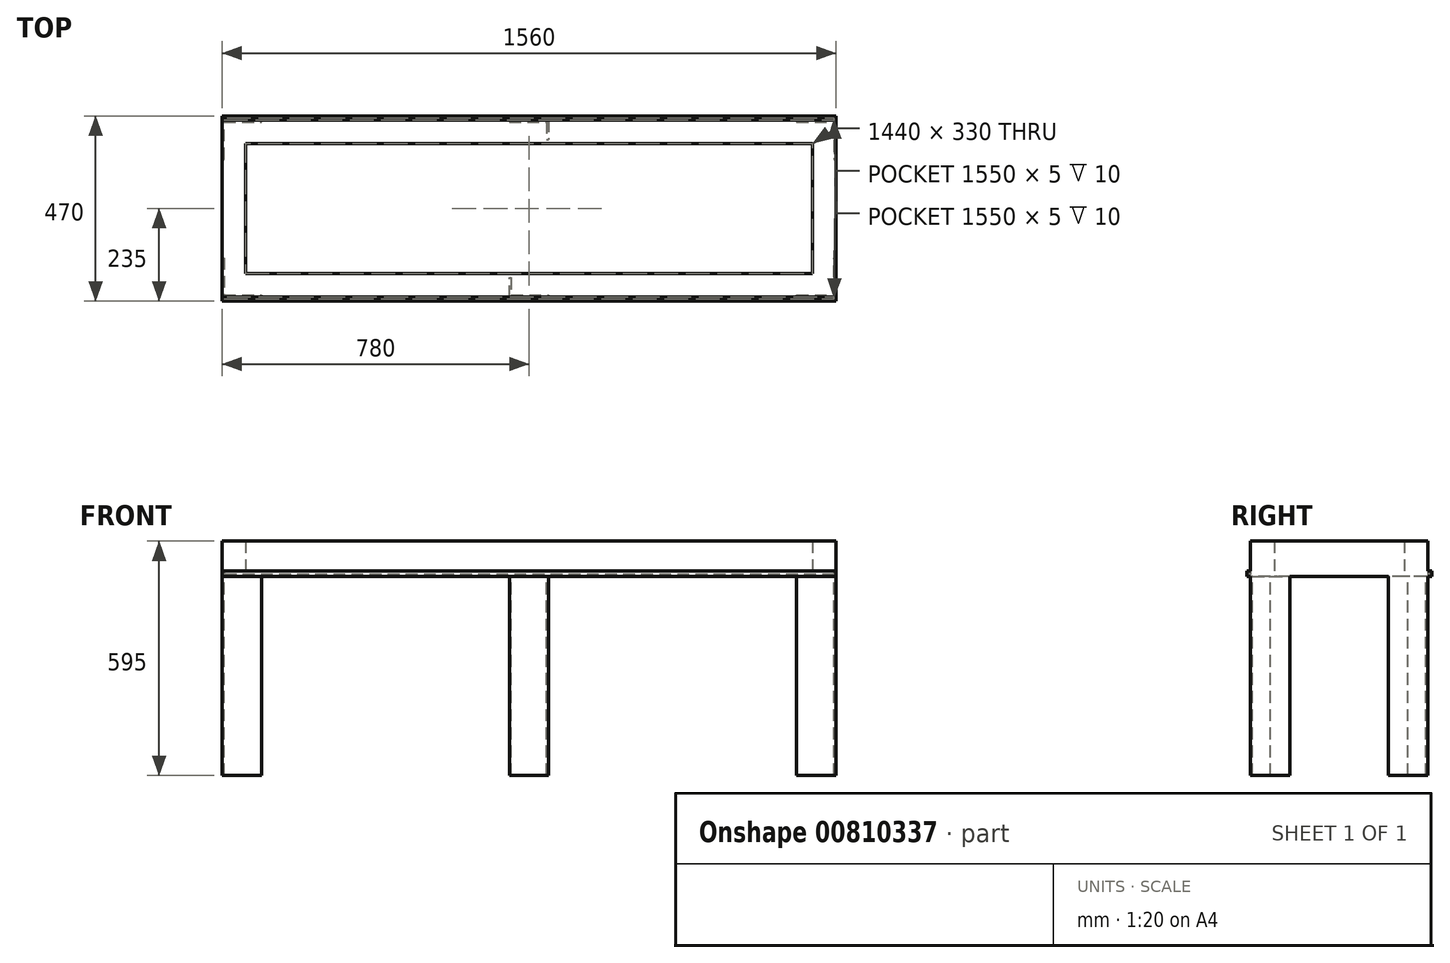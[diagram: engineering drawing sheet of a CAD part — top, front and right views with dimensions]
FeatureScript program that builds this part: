
annotation { "Feature Type Name" : "Feature", "Feature Type Description" : "" }
export const myFeature = defineFeature(function(context is Context, id is Id, definition is map)
    precondition{}
    {
        {
            var Q0;
            Q0=qCreatedBy(makeId("Top.planeOp"),FACE);
            var sketch = newSketch(context, id + "F0", { "sketchPlane" : qUnion([Q0])});
            skLineSegment(sketch, "E0", {"start": v(0, 526.95) * mm, "end": v(0, -464.95) * mm, "construction": true});
            skLineSegment(sketch, "E1", {"start": v(-587.5, 0) * mm, "end": v(637.96, 0) * mm, "construction": true});
            skLineSegment(sketch, "E2.bottom", {"start": v(-780, 225) * mm, "end": v(780, 225) * mm});
            skLineSegment(sketch, "E2.top", {"start": v(-780, -225) * mm, "end": v(780, -225) * mm});
            skLineSegment(sketch, "E2.left", {"start": v(-780, 225) * mm, "end": v(-780, -225) * mm});
            skLineSegment(sketch, "E2.right", {"start": v(780, 225) * mm, "end": v(780, -225) * mm});
            skLineSegment(sketch, "E3.0", {"start": v(-720, -165) * mm, "end": v(720, -165) * mm});
            skLineSegment(sketch, "E3.1", {"start": v(-720, 165) * mm, "end": v(-720, -165) * mm});
            skLineSegment(sketch, "E3.2", {"start": v(-720, 165) * mm, "end": v(720, 165) * mm});
            skLineSegment(sketch, "E3.3", {"start": v(720, 165) * mm, "end": v(720, -165) * mm});
            skSolve(sketch);
        }
        {
            var Q0;
            Q0 = qSketchRegion(id + "F0", true);
            extrude(context, id + "F1", {"entities" : qUnion([Q0]), "depth" : 90 * mm, "offsetDistance" : 25.4 * mm});
        }
        {
            var Q0;
            Q0=makeQuery(id+"F1.opExtrude","CAP_FACE",FACE,{"disambiguationData":[OSD([sQuery(id+"F0.wireOp",EDGE,"E2.bottom"),sQuery(id+"F0.wireOp",EDGE,"E2.top"),sQuery(id+"F0.wireOp",EDGE,"E2.left"),sQuery(id+"F0.wireOp",EDGE,"E2.right")])],"isStart":true});
            var sketch = newSketch(context, id + "F2", { "sketchPlane" : qUnion([Q0])});
            skLineSegment(sketch, "E4", {"start": v(-780, 125) * mm, "end": v(-780, 225) * mm});
            skLineSegment(sketch, "E5", {"start": v(-780, 225) * mm, "end": v(-680, 225) * mm});
            skLineSegment(sketch, "E6", {"start": v(-780, 125) * mm, "end": v(-775, 125) * mm});
            skLineSegment(sketch, "E7", {"start": v(-775, 125) * mm, "end": v(-775, 220) * mm});
            skLineSegment(sketch, "E8", {"start": v(-775, 220) * mm, "end": v(-680, 220) * mm});
            skLineSegment(sketch, "E9", {"start": v(-680, 220) * mm, "end": v(-680, 225) * mm});
            skLineSegment(sketch, "E10", {"start": v(-780, -125) * mm, "end": v(-780, -225) * mm});
            skLineSegment(sketch, "E11", {"start": v(-780, -225) * mm, "end": v(-680, -225) * mm});
            skLineSegment(sketch, "E12", {"start": v(-780, -125) * mm, "end": v(-775, -125) * mm});
            skLineSegment(sketch, "E13", {"start": v(-775, -125) * mm, "end": v(-775, -220) * mm});
            skLineSegment(sketch, "E14", {"start": v(-775, -220) * mm, "end": v(-680, -220) * mm});
            skLineSegment(sketch, "E15", {"start": v(-680, -220) * mm, "end": v(-680, -225) * mm});
            skLineSegment(sketch, "E16", {"start": v(0, 284.77) * mm, "end": v(0, -302.96) * mm, "construction": true});
            skLineSegment(sketch, "E17", {"start": v(-50, 225) * mm, "end": v(50, 225) * mm});
            skLineSegment(sketch, "E18", {"start": v(-50, 225) * mm, "end": v(-50, 175) * mm});
            skLineSegment(sketch, "E19", {"start": v(-50, 175) * mm, "end": v(-45, 175) * mm});
            skLineSegment(sketch, "E20", {"start": v(-45, 175) * mm, "end": v(-45, 220) * mm});
            skLineSegment(sketch, "E21", {"start": v(-45, 220) * mm, "end": v(50, 220) * mm});
            skLineSegment(sketch, "E22", {"start": v(50, 220) * mm, "end": v(50, 225) * mm});
            skLineSegment(sketch, "E23", {"start": v(-50, -225) * mm, "end": v(50, -225) * mm});
            skLineSegment(sketch, "E24", {"start": v(50, -225) * mm, "end": v(50, -175) * mm});
            skLineSegment(sketch, "E25", {"start": v(-50, -225) * mm, "end": v(-50, -220) * mm});
            skLineSegment(sketch, "E26", {"start": v(-50, -220) * mm, "end": v(45, -220) * mm});
            skLineSegment(sketch, "E27", {"start": v(45, -220) * mm, "end": v(45, -175) * mm});
            skLineSegment(sketch, "E28", {"start": v(45, -175) * mm, "end": v(50, -175) * mm});
            skLineSegment(sketch, "E29", {"start": v(680, 225) * mm, "end": v(780, 225) * mm});
            skLineSegment(sketch, "E30", {"start": v(780, 225) * mm, "end": v(780, 125) * mm});
            skLineSegment(sketch, "E31", {"start": v(680, 225) * mm, "end": v(680, 220) * mm});
            skLineSegment(sketch, "E32", {"start": v(680, 220) * mm, "end": v(775, 220) * mm});
            skLineSegment(sketch, "E33", {"start": v(775, 220) * mm, "end": v(775, 125) * mm});
            skLineSegment(sketch, "E34", {"start": v(775, 125) * mm, "end": v(780, 125) * mm});
            skLineSegment(sketch, "E35", {"start": v(680, -225) * mm, "end": v(780, -225) * mm});
            skLineSegment(sketch, "E36", {"start": v(780, -225) * mm, "end": v(780, -125) * mm});
            skLineSegment(sketch, "E37", {"start": v(680, -225) * mm, "end": v(680, -220) * mm});
            skLineSegment(sketch, "E38", {"start": v(680, -220) * mm, "end": v(775, -220) * mm});
            skLineSegment(sketch, "E39", {"start": v(775, -220) * mm, "end": v(775, -125) * mm});
            skLineSegment(sketch, "E40", {"start": v(775, -125) * mm, "end": v(780, -125) * mm});
            skSolve(sketch);
        }
        {
            var Q0;
            Q0 = qSketchRegion(id + "F2", true);
            extrude(context, id + "F3", {"entities" : qUnion([Q0]), "operationType" : NewBodyOperationType.ADD, "depth" : 505 * mm, "offsetDistance" : 25.4 * mm});
        }
        {
            var Q0;
            Q0=makeQuery(id+"F3.boolean.opBoolean","MERGE",FACE,{"derivedFrom":[makeQuery(id+"F1.opExtrude","SWEPT_FACE",FACE,{"disambiguationData":[OSD([sQuery(id+"F0.wireOp",EDGE,"E2.top")])]}),makeQuery(id+"F3.opExtrude","SWEPT_FACE",FACE,{"disambiguationData":[OSD([sQuery(id+"F2.wireOp",EDGE,"E5")])]}),makeQuery(id+"F3.opExtrude","SWEPT_FACE",FACE,{"disambiguationData":[OSD([sQuery(id+"F2.wireOp",EDGE,"E17")])]}),makeQuery(id+"F3.opExtrude","SWEPT_FACE",FACE,{"disambiguationData":[OSD([sQuery(id+"F2.wireOp",EDGE,"E29")])]})]});
            var sketch = newSketch(context, id + "F4", { "sketchPlane" : qUnion([Q0])});
            skLineSegment(sketch, "E41.bottom", {"start": v(-780, 0) * mm, "end": v(780, 0) * mm});
            skLineSegment(sketch, "E41.top", {"start": v(-780, 5) * mm, "end": v(780, 5) * mm});
            skLineSegment(sketch, "E41.left", {"start": v(-780, 0) * mm, "end": v(-780, 5) * mm});
            skLineSegment(sketch, "E41.right", {"start": v(780, 0) * mm, "end": v(780, 5) * mm});
            skSolve(sketch);
        }
        {
            var Q0;
            Q0=makeQuery(id+"F3.boolean.opBoolean","MERGE",FACE,{"derivedFrom":[makeQuery(id+"F1.opExtrude","SWEPT_FACE",FACE,{"disambiguationData":[OSD([sQuery(id+"F0.wireOp",EDGE,"E2.bottom")])]}),makeQuery(id+"F3.opExtrude","SWEPT_FACE",FACE,{"disambiguationData":[OSD([sQuery(id+"F2.wireOp",EDGE,"E11")])]}),makeQuery(id+"F3.opExtrude","SWEPT_FACE",FACE,{"disambiguationData":[OSD([sQuery(id+"F2.wireOp",EDGE,"E23")])]}),makeQuery(id+"F3.opExtrude","SWEPT_FACE",FACE,{"disambiguationData":[OSD([sQuery(id+"F2.wireOp",EDGE,"E35")])]})]});
            var sketch = newSketch(context, id + "F5", { "sketchPlane" : qUnion([Q0])});
            skLineSegment(sketch, "E42.bottom", {"start": v(-780, 0) * mm, "end": v(780, 0) * mm});
            skLineSegment(sketch, "E42.top", {"start": v(-780, 5) * mm, "end": v(780, 5) * mm});
            skLineSegment(sketch, "E42.left", {"start": v(-780, 0) * mm, "end": v(-780, 5) * mm});
            skLineSegment(sketch, "E42.right", {"start": v(780, 0) * mm, "end": v(780, 5) * mm});
            skSolve(sketch);
        }
        {
            var Q0;
            Q0 = qSketchRegion(id + "F4", true);
            extrude(context, id + "F6", {"entities" : qUnion([Q0]), "operationType" : NewBodyOperationType.ADD, "depth" : 10 * mm, "offsetDistance" : 25.4 * mm});
        }
        {
            var Q0;
            Q0 = qSketchRegion(id + "F5", true);
            extrude(context, id + "F7", {"entities" : qUnion([Q0]), "operationType" : NewBodyOperationType.ADD, "depth" : 10 * mm, "offsetDistance" : 25.4 * mm});
        }
        {
            var Q0;
            Q0=makeQuery(id+"F6.opExtrude","SWEPT_FACE",FACE,{"disambiguationData":[OSD([sQuery(id+"F4.wireOp",EDGE,"E41.top")])]});
            var sketch = newSketch(context, id + "F8", { "sketchPlane" : qUnion([Q0])});
            skLineSegment(sketch, "E43.bottom", {"start": v(-780, -235) * mm, "end": v(780, -235) * mm});
            skLineSegment(sketch, "E43.top", {"start": v(-775, -230) * mm, "end": v(775, -230) * mm});
            skLineSegment(sketch, "E43.left", {"start": v(-780, -235) * mm, "end": v(-780, -230) * mm});
            skLineSegment(sketch, "E43.right", {"start": v(780, -235) * mm, "end": v(780, -230) * mm});
            skLineSegment(sketch, "E44.bottom", {"start": v(780, -235) * mm, "end": v(775, -235) * mm});
            skLineSegment(sketch, "E44.top", {"start": v(780, -225) * mm, "end": v(775, -225) * mm});
            skLineSegment(sketch, "E44.left", {"start": v(780, -230) * mm, "end": v(780, -225) * mm});
            skLineSegment(sketch, "E44.right", {"start": v(775, -230) * mm, "end": v(775, -225) * mm});
            skLineSegment(sketch, "E45.bottom", {"start": v(-780, -235) * mm, "end": v(-775, -235) * mm});
            skLineSegment(sketch, "E45.top", {"start": v(-780, -225) * mm, "end": v(-775, -225) * mm});
            skLineSegment(sketch, "E45.left", {"start": v(-780, -235) * mm, "end": v(-780, -225) * mm});
            skLineSegment(sketch, "E45.right", {"start": v(-775, -230) * mm, "end": v(-775, -225) * mm});
            skSolve(sketch);
        }
        {
            var Q0;
            Q0 = qSketchRegion(id + "F8", true);
            extrude(context, id + "F9", {"entities" : qUnion([Q0]), "operationType" : NewBodyOperationType.ADD, "depth" : 10 * mm, "offsetDistance" : 25.4 * mm});
        }
        {
            var Q0;
            Q0=makeQuery(id+"F7.opExtrude","SWEPT_FACE",FACE,{"disambiguationData":[OSD([sQuery(id+"F5.wireOp",EDGE,"E42.top")])]});
            var sketch = newSketch(context, id + "F10", { "sketchPlane" : qUnion([Q0])});
            skLineSegment(sketch, "E46.bottom", {"start": v(-780, 225) * mm, "end": v(-775, 225) * mm});
            skLineSegment(sketch, "E46.top", {"start": v(-780, 235) * mm, "end": v(-775, 235) * mm});
            skLineSegment(sketch, "E46.left", {"start": v(-780, 225) * mm, "end": v(-780, 235) * mm});
            skLineSegment(sketch, "E46.right", {"start": v(-775, 225) * mm, "end": v(-775, 230) * mm});
            skLineSegment(sketch, "E47.bottom", {"start": v(-775, 235) * mm, "end": v(780, 235) * mm});
            skLineSegment(sketch, "E47.top", {"start": v(-775, 230) * mm, "end": v(775, 230) * mm});
            skLineSegment(sketch, "E47.right", {"start": v(780, 235) * mm, "end": v(780, 230) * mm});
            skLineSegment(sketch, "E48.top", {"start": v(780, 225) * mm, "end": v(775, 225) * mm});
            skLineSegment(sketch, "E48.left", {"start": v(780, 230) * mm, "end": v(780, 225) * mm});
            skLineSegment(sketch, "E48.right", {"start": v(775, 230) * mm, "end": v(775, 225) * mm});
            skSolve(sketch);
        }
        {
            var Q0;
            Q0 = qSketchRegion(id + "F10", true);
            extrude(context, id + "F11", {"entities" : qUnion([Q0]), "operationType" : NewBodyOperationType.ADD, "depth" : 10 * mm, "offsetDistance" : 25.4 * mm});
        }
    });
